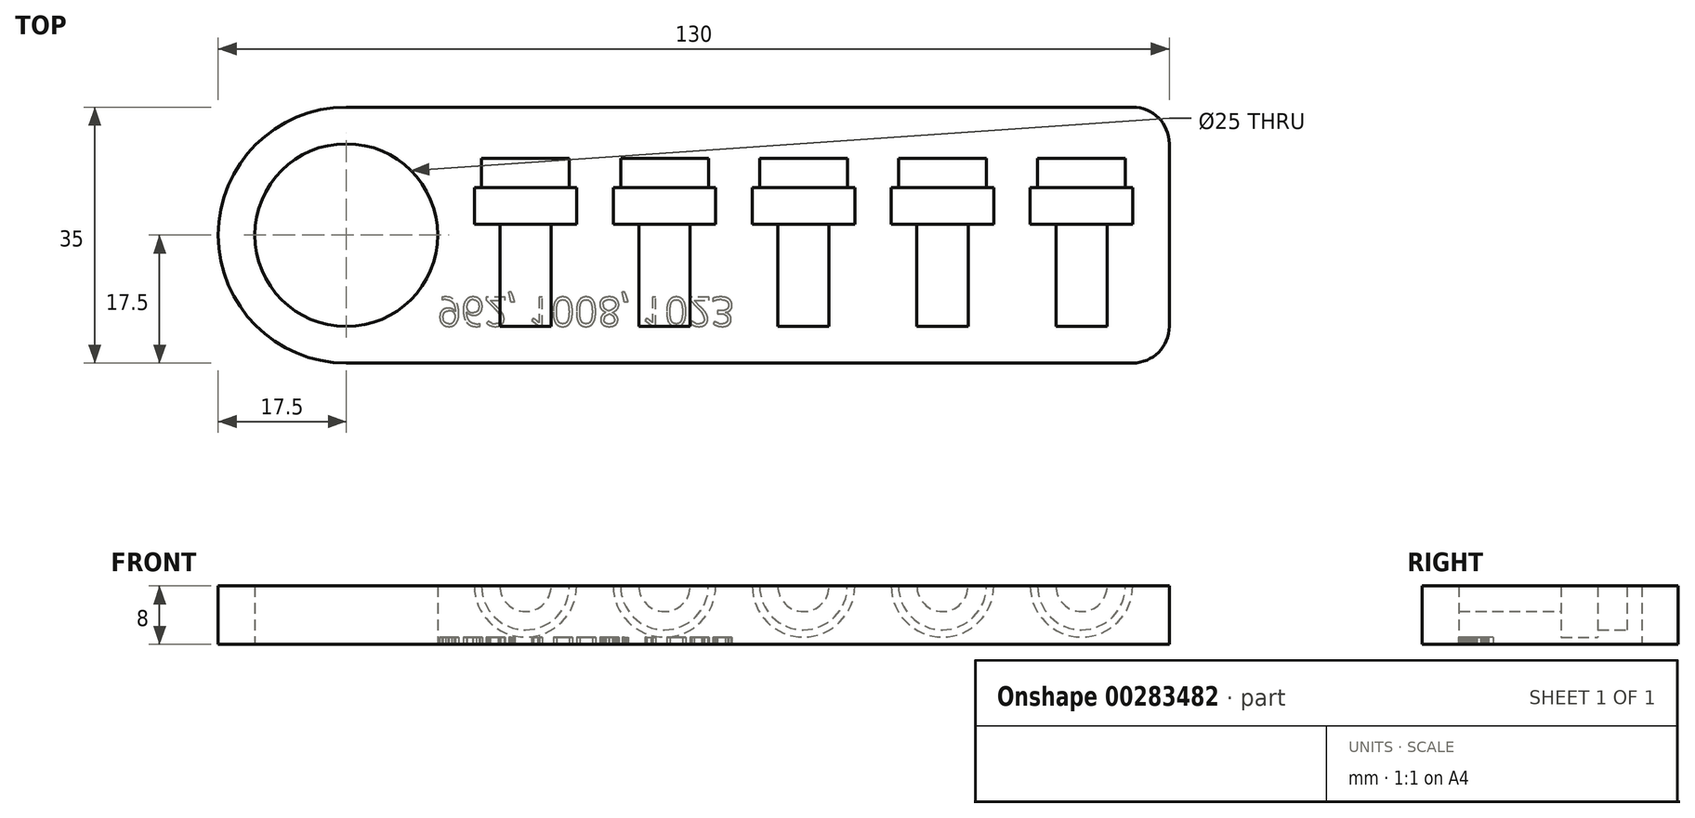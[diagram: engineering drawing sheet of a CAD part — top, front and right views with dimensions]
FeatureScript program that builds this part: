
annotation { "Feature Type Name" : "Feature", "Feature Type Description" : "" }
export const myFeature = defineFeature(function(context is Context, id is Id, definition is map)
    precondition{}
    {
        {
            var Q0;
            Q0=qCreatedBy(makeId("Top.planeOp"),FACE);
            var sketch = newSketch(context, id + "F0", { "sketchPlane" : qUnion([Q0])});
            skLineSegment(sketch, "E0.bottom", {"start": v(17.5, 0) * mm, "end": v(125, 0) * mm});
            skLineSegment(sketch, "E0.top", {"start": v(17.5, 35) * mm, "end": v(125, 35) * mm});
            skLineSegment(sketch, "E0.left", {"start": v(0, 17.5) * mm, "end": v(0, 17.5) * mm});
            skLineSegment(sketch, "E0.right", {"start": v(130, 5) * mm, "end": v(130, 30) * mm});
            skLineSegment(sketch, "E1.bottom", {"start": v(0, 0) * mm, "end": v(17.5, 0) * mm, "construction": true});
            skLineSegment(sketch, "E1.top", {"start": v(0, 17.5) * mm, "end": v(17.5, 17.5) * mm, "construction": true});
            skLineSegment(sketch, "E1.left", {"start": v(0, 0) * mm, "end": v(0, 17.5) * mm, "construction": true});
            skLineSegment(sketch, "E1.right", {"start": v(17.5, 0) * mm, "end": v(17.5, 17.5) * mm, "construction": true});
            skCircle(sketch, "E2", {"center": v(17.5, 17.5) * mm, "radius": 12.5 * mm});
            skPoint(sketch, "E3.visualSharp", {"position": v(0, 0) * mm});
            skArc(sketch, "E3.filletArc", {"start": v(0, 17.5) * mm, "mid": v(5.13, 5.13) * mm, "end": v(17.5, 0) * mm});
            skPoint(sketch, "E4.visualSharp", {"position": v(0, 35) * mm});
            skArc(sketch, "E4.filletArc", {"start": v(17.5, 35) * mm, "mid": v(5.13, 29.87) * mm, "end": v(0, 17.5) * mm});
            skPoint(sketch, "E5.visualSharp", {"position": v(130, 35) * mm});
            skArc(sketch, "E5.filletArc", {"start": v(130, 30) * mm, "mid": v(128.54, 33.54) * mm, "end": v(125, 35) * mm});
            skPoint(sketch, "E6.visualSharp", {"position": v(130, 0) * mm});
            skArc(sketch, "E6.filletArc", {"start": v(125, 0) * mm, "mid": v(128.54, 1.46) * mm, "end": v(130, 5) * mm});
            skSolve(sketch);
        }
        {
            var Q0;
            Q0=makeQuery(id+"F0.imprint","IMPRINT",FACE,{"disambiguationData":[TD([[makeQuery(id+"F0.imprint","IMPRINT",EDGE,{"derivedFrom":sQuery(id+"F0.wireOp",EDGE,"E0.bottom")}),1.0]])]});
            extrude(context, id + "F1", {"entities" : qUnion([Q0]), "depth" : 8 * mm});
        }
        {
            var Q0;
            Q0=makeQuery(id+"F1.opExtrude","CAP_FACE",FACE,{"disambiguationData":[OSD([sQuery(id+"F0.wireOp",EDGE,"E0.bottom"),sQuery(id+"F0.wireOp",EDGE,"E0.top"),sQuery(id+"F0.wireOp",EDGE,"E0.right"),sQuery(id+"F0.wireOp",EDGE,"E2"),sQuery(id+"F0.wireOp",EDGE,"E3.filletArc"),sQuery(id+"F0.wireOp",EDGE,"E4.filletArc"),sQuery(id+"F0.wireOp",EDGE,"E5.filletArc"),sQuery(id+"F0.wireOp",EDGE,"E6.filletArc")])],"isStart":false});
            var sketch = newSketch(context, id + "F2", { "sketchPlane" : qUnion([Q0])});
            skLineSegment(sketch, "E7.bottom", {"start": v(0, 0) * mm, "end": v(42, 0) * mm, "construction": true});
            skLineSegment(sketch, "E7.top", {"start": v(0, 5) * mm, "end": v(42, 5) * mm, "construction": true});
            skLineSegment(sketch, "E7.left", {"start": v(0, 0) * mm, "end": v(0, 5) * mm, "construction": true});
            skLineSegment(sketch, "E7.right", {"start": v(42, 0) * mm, "end": v(42, 5) * mm, "construction": true});
            skLineSegment(sketch, "E8", {"start": v(42, 5) * mm, "end": v(61, 5) * mm, "construction": true});
            skLineSegment(sketch, "E9", {"start": v(61, 5) * mm, "end": v(80, 5) * mm, "construction": true});
            skLineSegment(sketch, "E10", {"start": v(80, 5) * mm, "end": v(99, 5) * mm, "construction": true});
            skLineSegment(sketch, "E11.bottom", {"start": v(42, 5) * mm, "end": v(45.5, 5) * mm});
            skLineSegment(sketch, "E11.left", {"start": v(42, 5) * mm, "end": v(42, 19) * mm});
            skLineSegment(sketch, "E11.right", {"start": v(45.5, 5) * mm, "end": v(45.5, 19) * mm});
            skLineSegment(sketch, "E12.bottom", {"start": v(45.5, 19) * mm, "end": v(49, 19) * mm});
            skLineSegment(sketch, "E12.top", {"start": v(48, 24) * mm, "end": v(49, 24) * mm});
            skLineSegment(sketch, "E12.left", {"start": v(42, 19) * mm, "end": v(42, 24) * mm});
            skLineSegment(sketch, "E12.right", {"start": v(49, 19) * mm, "end": v(49, 24) * mm});
            skLineSegment(sketch, "E13.top", {"start": v(42, 28) * mm, "end": v(48, 28) * mm});
            skLineSegment(sketch, "E13.left", {"start": v(42, 24) * mm, "end": v(42, 28) * mm});
            skLineSegment(sketch, "E13.right", {"start": v(48, 24) * mm, "end": v(48, 28) * mm});
            skLineSegment(sketch, "E14.bottom", {"start": v(61, 5) * mm, "end": v(64.5, 5) * mm});
            skLineSegment(sketch, "E14.left", {"start": v(61, 5) * mm, "end": v(61, 19) * mm});
            skLineSegment(sketch, "E14.right", {"start": v(64.5, 5) * mm, "end": v(64.5, 19) * mm});
            skLineSegment(sketch, "E15.bottom", {"start": v(64.5, 19) * mm, "end": v(68, 19) * mm});
            skLineSegment(sketch, "E15.top", {"start": v(67, 24) * mm, "end": v(68, 24) * mm});
            skLineSegment(sketch, "E15.left", {"start": v(61, 19) * mm, "end": v(61, 24) * mm});
            skLineSegment(sketch, "E15.right", {"start": v(68, 19) * mm, "end": v(68, 24) * mm});
            skLineSegment(sketch, "E16.top", {"start": v(61, 28) * mm, "end": v(67, 28) * mm});
            skLineSegment(sketch, "E16.left", {"start": v(61, 24) * mm, "end": v(61, 28) * mm});
            skLineSegment(sketch, "E16.right", {"start": v(67, 24) * mm, "end": v(67, 28) * mm});
            skLineSegment(sketch, "E17.bottom", {"start": v(80, 5) * mm, "end": v(83.5, 5) * mm});
            skLineSegment(sketch, "E17.left", {"start": v(80, 5) * mm, "end": v(80, 19) * mm});
            skLineSegment(sketch, "E17.right", {"start": v(83.5, 5) * mm, "end": v(83.5, 19) * mm});
            skLineSegment(sketch, "E18.bottom", {"start": v(83.5, 19) * mm, "end": v(87, 19) * mm});
            skLineSegment(sketch, "E18.top", {"start": v(86, 24) * mm, "end": v(87, 24) * mm});
            skLineSegment(sketch, "E18.left", {"start": v(80, 19) * mm, "end": v(80, 24) * mm});
            skLineSegment(sketch, "E18.right", {"start": v(87, 19) * mm, "end": v(87, 24) * mm});
            skLineSegment(sketch, "E19.top", {"start": v(80, 28) * mm, "end": v(86, 28) * mm});
            skLineSegment(sketch, "E19.left", {"start": v(80, 24) * mm, "end": v(80, 28) * mm});
            skLineSegment(sketch, "E19.right", {"start": v(86, 24) * mm, "end": v(86, 28) * mm});
            skLineSegment(sketch, "E20.bottom", {"start": v(99, 5) * mm, "end": v(102.5, 5) * mm});
            skLineSegment(sketch, "E20.left", {"start": v(99, 5) * mm, "end": v(99, 19) * mm});
            skLineSegment(sketch, "E20.right", {"start": v(102.5, 5) * mm, "end": v(102.5, 19) * mm});
            skLineSegment(sketch, "E21.bottom", {"start": v(102.5, 19) * mm, "end": v(106, 19) * mm});
            skLineSegment(sketch, "E21.top", {"start": v(105, 24) * mm, "end": v(106, 24) * mm});
            skLineSegment(sketch, "E21.left", {"start": v(99, 19) * mm, "end": v(99, 24) * mm});
            skLineSegment(sketch, "E21.right", {"start": v(106, 19) * mm, "end": v(106, 24) * mm});
            skLineSegment(sketch, "E22.top", {"start": v(99, 28) * mm, "end": v(105, 28) * mm});
            skLineSegment(sketch, "E22.left", {"start": v(99, 24) * mm, "end": v(99, 28) * mm});
            skLineSegment(sketch, "E22.right", {"start": v(105, 24) * mm, "end": v(105, 28) * mm});
            skLineSegment(sketch, "E23", {"start": v(99, 5) * mm, "end": v(118, 5) * mm, "construction": true});
            skLineSegment(sketch, "E24.bottom", {"start": v(118, 5) * mm, "end": v(121.5, 5) * mm});
            skLineSegment(sketch, "E24.left", {"start": v(118, 5) * mm, "end": v(118, 19) * mm});
            skLineSegment(sketch, "E24.right", {"start": v(121.5, 5) * mm, "end": v(121.5, 19) * mm});
            skLineSegment(sketch, "E25.bottom", {"start": v(121.5, 19) * mm, "end": v(125, 19) * mm});
            skLineSegment(sketch, "E25.top", {"start": v(124, 24) * mm, "end": v(125, 24) * mm});
            skLineSegment(sketch, "E25.left", {"start": v(118, 19) * mm, "end": v(118, 24) * mm});
            skLineSegment(sketch, "E25.right", {"start": v(125, 19) * mm, "end": v(125, 24) * mm});
            skLineSegment(sketch, "E26.top", {"start": v(118, 28) * mm, "end": v(124, 28) * mm});
            skLineSegment(sketch, "E26.left", {"start": v(118, 24) * mm, "end": v(118, 28) * mm});
            skLineSegment(sketch, "E26.right", {"start": v(124, 24) * mm, "end": v(124, 28) * mm});
            skSolve(sketch);
        }
        {
            var Q0;
            Q0=makeQuery(id+"F2.imprint","IMPRINT",FACE,{"disambiguationData":[TD([[makeQuery(id+"F2.imprint","IMPRINT",EDGE,{"derivedFrom":sQuery(id+"F2.wireOp",EDGE,"E11.bottom")}),1.0]])]});
            var Q1;
            Q1=sQuery(id+"F2.wireOp",EDGE,"E12.left");
            revolve(context, id + "F3", {"operationType" : NewBodyOperationType.REMOVE, "entities" : qUnion([Q0]), "axis" : qUnion([Q1]), "revolveType" : RevolveType.FULL, "oppositeDirection" : true});
        }
        {
            var Q0;
            Q0=makeQuery(id+"F2.imprint","IMPRINT",FACE,{"disambiguationData":[TD([[makeQuery(id+"F2.imprint","IMPRINT",EDGE,{"derivedFrom":sQuery(id+"F2.wireOp",EDGE,"E14.bottom")}),1.0]])]});
            var Q1;
            Q1=sQuery(id+"F2.wireOp",EDGE,"E15.left");
            revolve(context, id + "F4", {"operationType" : NewBodyOperationType.REMOVE, "entities" : qUnion([Q0]), "axis" : qUnion([Q1]), "revolveType" : RevolveType.FULL, "oppositeDirection" : true});
        }
        {
            var Q0;
            Q0=makeQuery(id+"F2.imprint","IMPRINT",FACE,{"disambiguationData":[TD([[makeQuery(id+"F2.imprint","IMPRINT",EDGE,{"derivedFrom":sQuery(id+"F2.wireOp",EDGE,"E17.bottom")}),1.0]])]});
            var Q1;
            Q1=sQuery(id+"F2.wireOp",EDGE,"E17.left");
            revolve(context, id + "F5", {"operationType" : NewBodyOperationType.REMOVE, "entities" : qUnion([Q0]), "axis" : qUnion([Q1]), "revolveType" : RevolveType.FULL, "oppositeDirection" : true});
        }
        {
            var Q0;
            Q0=makeQuery(id+"F2.imprint","IMPRINT",FACE,{"disambiguationData":[TD([[makeQuery(id+"F2.imprint","IMPRINT",EDGE,{"derivedFrom":sQuery(id+"F2.wireOp",EDGE,"E20.bottom")}),1.0]])]});
            var Q1;
            Q1=sQuery(id+"F2.wireOp",EDGE,"E20.left");
            revolve(context, id + "F6", {"operationType" : NewBodyOperationType.REMOVE, "entities" : qUnion([Q0]), "axis" : qUnion([Q1]), "revolveType" : RevolveType.FULL, "oppositeDirection" : true});
        }
        {
            var Q0;
            Q0=makeQuery(id+"F2.imprint","IMPRINT",FACE,{"disambiguationData":[TD([[makeQuery(id+"F2.imprint","IMPRINT",EDGE,{"derivedFrom":sQuery(id+"F2.wireOp",EDGE,"E24.bottom")}),1.0]])]});
            var Q1;
            Q1=sQuery(id+"F2.wireOp",EDGE,"E24.left");
            revolve(context, id + "F7", {"operationType" : NewBodyOperationType.REMOVE, "entities" : qUnion([Q0]), "axis" : qUnion([Q1]), "revolveType" : RevolveType.FULL, "oppositeDirection" : true});
        }
        {
            var Q0;
            Q0=makeQuery(id+"F1.opExtrude","CAP_FACE",FACE,{"disambiguationData":[OSD([sQuery(id+"F0.wireOp",EDGE,"E0.bottom"),sQuery(id+"F0.wireOp",EDGE,"E0.top"),sQuery(id+"F0.wireOp",EDGE,"E0.right"),sQuery(id+"F0.wireOp",EDGE,"E2"),sQuery(id+"F0.wireOp",EDGE,"E3.filletArc"),sQuery(id+"F0.wireOp",EDGE,"E4.filletArc"),sQuery(id+"F0.wireOp",EDGE,"E5.filletArc"),sQuery(id+"F0.wireOp",EDGE,"E6.filletArc")])],"isStart":true});
            var sketch = newSketch(context, id + "F8", { "sketchPlane" : qUnion([Q0])});
            skLineSegment(sketch, "E27.bottom", {"start": v(0, 0) * mm, "end": v(30, 0) * mm, "construction": true});
            skLineSegment(sketch, "E27.top", {"start": v(0, -5) * mm, "end": v(30, -5) * mm, "construction": true});
            skLineSegment(sketch, "E27.left", {"start": v(0, 0) * mm, "end": v(0, -5) * mm, "construction": true});
            skLineSegment(sketch, "E27.right", {"start": v(30, 0) * mm, "end": v(30, -5) * mm, "construction": true});
            skText(sketch, "E28", { "text": "962, 1008, 1023", "fontName": "OpenSans-Regular.ttf"});
            const initialGuessF8  = {"E28": [0.03, -0.009, 1, 0, 0.004]};
            skSetInitialGuess(sketch, initialGuessF8);
            skSolve(sketch);
        }
        {
            var Q0;
            Q0 = qSketchRegion(id + "F8", true);
            extrude(context, id + "F9", {"entities" : qUnion([Q0]), "operationType" : NewBodyOperationType.REMOVE, "oppositeDirection" : true, "depth" : 1 * mm});
        }
    });
